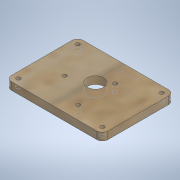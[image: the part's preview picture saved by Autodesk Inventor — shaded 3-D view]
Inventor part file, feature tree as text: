
AUTODESK INVENTOR PART (.ipt)
format: ipt  version: 2020.3 (Build 243373000, 373)  size: 159,232 bytes
history: native  units: mm
features: sketch x4, extrude x2, hole x2, other x1, fillet x1
ambient origin geometry x8: Origin, YZ Plane, XZ Plane, XY Plane, X Axis, Y Axis, Z Axis, Center Point
bodies: Body1 (feature_tree)
feature tree (10):
  other  "ソリッド1"
  extrude  "押し出し1"  Depth=5.5mm TaperAngle=0.0deg
  hole  "穴1"  [1 undecoded]
  fillet  "フィレット1"  Radius=57.0mm
  hole  "穴2"  [1 undecoded]
  extrude  "押し出し2"  Depth=4.5mm
  sketch  "スケッチ1"
  sketch  "スケッチ2"
  sketch  "スケッチ3"
  sketch  "スケッチ4"
note: 2 required parameter values undecoded (feature->parameter linkage not recoverable at this tier; creation-order binding heuristic only, values carry confidence <= 0.55)
